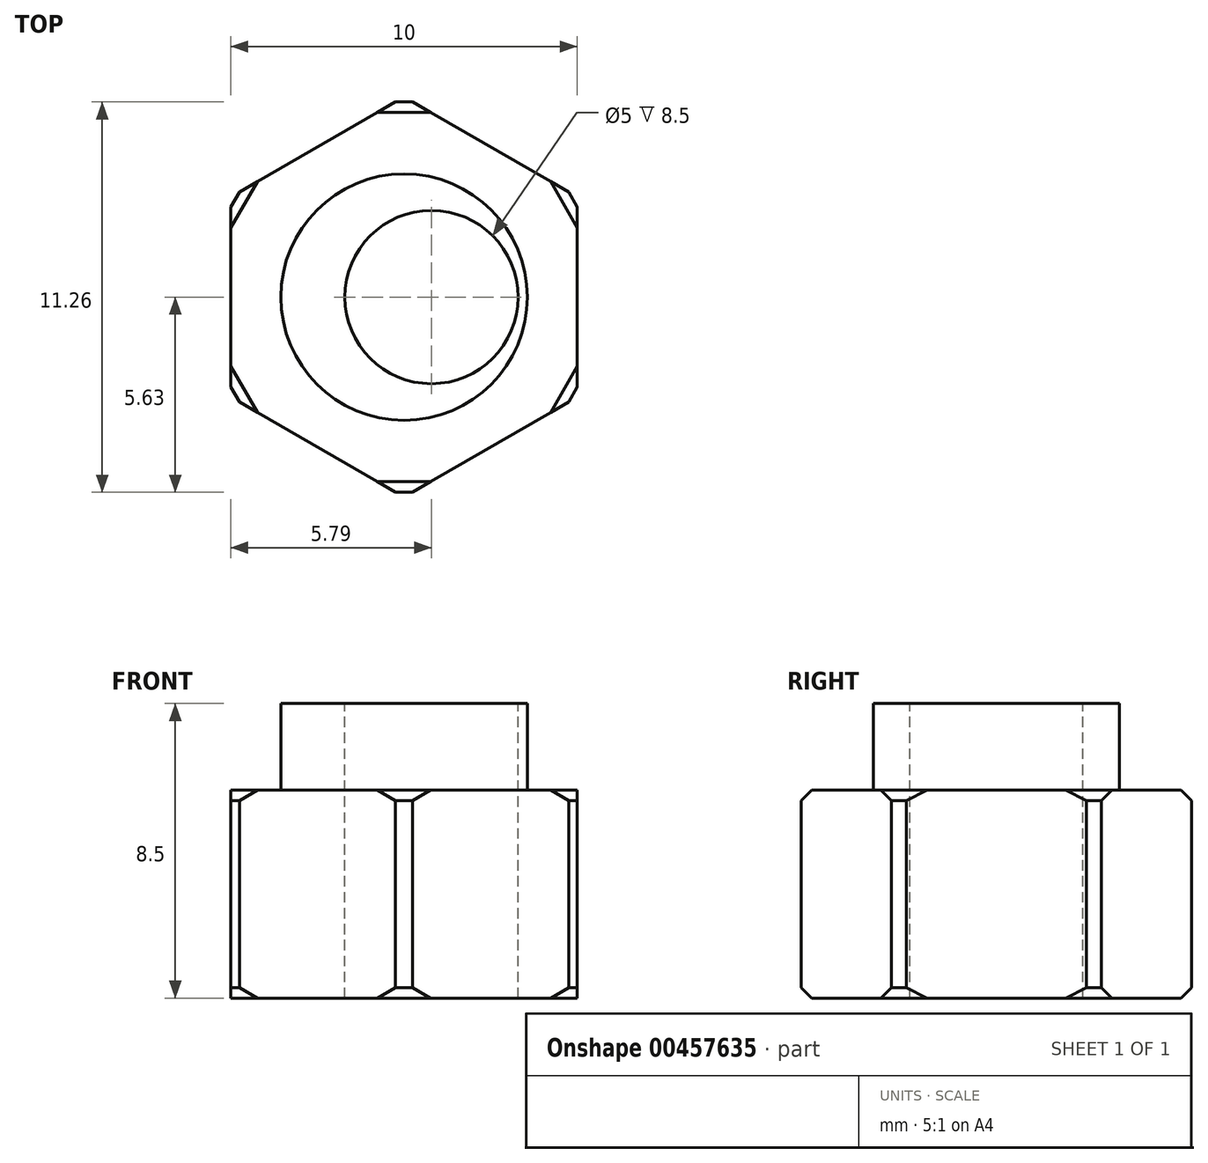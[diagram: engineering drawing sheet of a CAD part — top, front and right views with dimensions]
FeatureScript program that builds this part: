
annotation { "Feature Type Name" : "Feature", "Feature Type Description" : "" }
export const myFeature = defineFeature(function(context is Context, id is Id, definition is map)
    precondition{}
    {
        {
            var Q0;
            Q0=qCreatedBy(makeId("Top.planeOp"),FACE);
            var sketch = newSketch(context, id + "F0", { "sketchPlane" : qUnion([Q0])});
            skCircle(sketch, "E0.cCircle", {"center": v(0, 0) * mm, "radius": 5 * mm, "construction": true});
            skLineSegment(sketch, "E0.0", {"start": v(5, -2.89) * mm, "end": v(0, -5.77) * mm});
            skLineSegment(sketch, "E0.1", {"start": v(0, -5.77) * mm, "end": v(-5, -2.89) * mm});
            skLineSegment(sketch, "E0.2", {"start": v(-5, -2.89) * mm, "end": v(-5, 2.89) * mm});
            skLineSegment(sketch, "E0.3", {"start": v(-5, 2.89) * mm, "end": v(0, 5.77) * mm});
            skLineSegment(sketch, "E0.4", {"start": v(0, 5.77) * mm, "end": v(5, 2.89) * mm});
            skLineSegment(sketch, "E0.5", {"start": v(5, 2.89) * mm, "end": v(5, -2.89) * mm});
            skPoint(sketch, "E0.0.midPoint", {"position": v(2.5, -4.33) * mm});
            skSolve(sketch);
        }
        {
            var Q0;
            Q0=makeQuery(id+"F0.imprint","IMPRINT",FACE,{"disambiguationData":[TD([[makeQuery(id+"F0.imprint","IMPRINT",EDGE,{"derivedFrom":sQuery(id+"F0.wireOp",EDGE,"E0.0")}),-1.0]])]});
            extrude(context, id + "F1", {"entities" : qUnion([Q0]), "depth" : 6 * mm});
        }
        {
            var Q0;
            Q0=makeQuery(id+"F1.opExtrude","SWEPT_EDGE",EDGE,{"disambiguationData":[OSD([sQuery(id+"F0.wireOp",EDGE,"E0.4"),sQuery(id+"F0.wireOp",EDGE,"E0.5")])]});
            var Q1;
            Q1=makeQuery(id+"F1.opExtrude","SWEPT_EDGE",EDGE,{"disambiguationData":[OSD([sQuery(id+"F0.wireOp",EDGE,"E0.3"),sQuery(id+"F0.wireOp",EDGE,"E0.4")])]});
            var Q2;
            Q2=makeQuery(id+"F1.opExtrude","SWEPT_EDGE",EDGE,{"disambiguationData":[OSD([sQuery(id+"F0.wireOp",EDGE,"E0.0"),sQuery(id+"F0.wireOp",EDGE,"E0.5")])]});
            var Q3;
            Q3=makeQuery(id+"F1.opExtrude","SWEPT_EDGE",EDGE,{"disambiguationData":[OSD([sQuery(id+"F0.wireOp",EDGE,"E0.0"),sQuery(id+"F0.wireOp",EDGE,"E0.1")])]});
            var Q4;
            Q4=makeQuery(id+"F1.opExtrude","SWEPT_EDGE",EDGE,{"disambiguationData":[OSD([sQuery(id+"F0.wireOp",EDGE,"E0.1"),sQuery(id+"F0.wireOp",EDGE,"E0.2")])]});
            var Q5;
            Q5=makeQuery(id+"F1.opExtrude","SWEPT_EDGE",EDGE,{"disambiguationData":[OSD([sQuery(id+"F0.wireOp",EDGE,"E0.2"),sQuery(id+"F0.wireOp",EDGE,"E0.3")])]});
            chamfer(context, id + "F2", {"entities" : qUnion([Q0, Q1, Q2, Q3, Q4, Q5]), "width" : 0.5 * mm, "tangentPropagation" : true});
        }
        {
            var Q0;
            {var subQ0=sQuery(id+"F0.wireOp",EDGE,"E0.5");var subQ1=sQuery(id+"F0.wireOp",EDGE,"E0.4");Q0=makeQuery(id+"F2.opChamfer","BLEND_EDGE",EDGE,{"blendedFrom":[makeQuery(id+"F1.opExtrude","SWEPT_EDGE",EDGE,{"disambiguationData":[OSD([subQ1,subQ0])]}),makeQuery(id+"F1.opExtrude","CAP_FACE",FACE,{"disambiguationData":[OSD([sQuery(id+"F0.wireOp",EDGE,"E0.0"),sQuery(id+"F0.wireOp",EDGE,"E0.1"),sQuery(id+"F0.wireOp",EDGE,"E0.2"),sQuery(id+"F0.wireOp",EDGE,"E0.3"),subQ1,subQ0])],"isStart":false})],"blendedInto":[makeQuery(id+"F1.opExtrude","CAP_FACE",FACE,{"disambiguationData":[OSD([sQuery(id+"F0.wireOp",EDGE,"E0.0"),sQuery(id+"F0.wireOp",EDGE,"E0.1"),sQuery(id+"F0.wireOp",EDGE,"E0.2"),sQuery(id+"F0.wireOp",EDGE,"E0.3"),subQ1,subQ0])],"isStart":false})]});}
            var Q1;
            {var subQ0=sQuery(id+"F0.wireOp",EDGE,"E0.5");var subQ1=sQuery(id+"F0.wireOp",EDGE,"E0.0");Q1=makeQuery(id+"F2.opChamfer","BLEND_EDGE",EDGE,{"blendedFrom":[makeQuery(id+"F1.opExtrude","SWEPT_EDGE",EDGE,{"disambiguationData":[OSD([subQ1,subQ0])]}),makeQuery(id+"F1.opExtrude","CAP_FACE",FACE,{"disambiguationData":[OSD([subQ1,sQuery(id+"F0.wireOp",EDGE,"E0.1"),sQuery(id+"F0.wireOp",EDGE,"E0.2"),sQuery(id+"F0.wireOp",EDGE,"E0.3"),sQuery(id+"F0.wireOp",EDGE,"E0.4"),subQ0])],"isStart":false})],"blendedInto":[makeQuery(id+"F1.opExtrude","CAP_FACE",FACE,{"disambiguationData":[OSD([subQ1,sQuery(id+"F0.wireOp",EDGE,"E0.1"),sQuery(id+"F0.wireOp",EDGE,"E0.2"),sQuery(id+"F0.wireOp",EDGE,"E0.3"),sQuery(id+"F0.wireOp",EDGE,"E0.4"),subQ0])],"isStart":false})]});}
            var Q2;
            {var subQ0=sQuery(id+"F0.wireOp",EDGE,"E0.4");var subQ1=sQuery(id+"F0.wireOp",EDGE,"E0.3");Q2=makeQuery(id+"F2.opChamfer","BLEND_EDGE",EDGE,{"blendedFrom":[makeQuery(id+"F1.opExtrude","SWEPT_EDGE",EDGE,{"disambiguationData":[OSD([subQ1,subQ0])]}),makeQuery(id+"F1.opExtrude","CAP_FACE",FACE,{"disambiguationData":[OSD([sQuery(id+"F0.wireOp",EDGE,"E0.0"),sQuery(id+"F0.wireOp",EDGE,"E0.1"),sQuery(id+"F0.wireOp",EDGE,"E0.2"),subQ1,subQ0,sQuery(id+"F0.wireOp",EDGE,"E0.5")])],"isStart":false})],"blendedInto":[makeQuery(id+"F1.opExtrude","CAP_FACE",FACE,{"disambiguationData":[OSD([sQuery(id+"F0.wireOp",EDGE,"E0.0"),sQuery(id+"F0.wireOp",EDGE,"E0.1"),sQuery(id+"F0.wireOp",EDGE,"E0.2"),subQ1,subQ0,sQuery(id+"F0.wireOp",EDGE,"E0.5")])],"isStart":false})]});}
            var Q3;
            {var subQ0=sQuery(id+"F0.wireOp",EDGE,"E0.3");var subQ1=sQuery(id+"F0.wireOp",EDGE,"E0.2");Q3=makeQuery(id+"F2.opChamfer","BLEND_EDGE",EDGE,{"blendedFrom":[makeQuery(id+"F1.opExtrude","SWEPT_EDGE",EDGE,{"disambiguationData":[OSD([subQ1,subQ0])]}),makeQuery(id+"F1.opExtrude","CAP_FACE",FACE,{"disambiguationData":[OSD([sQuery(id+"F0.wireOp",EDGE,"E0.0"),sQuery(id+"F0.wireOp",EDGE,"E0.1"),subQ1,subQ0,sQuery(id+"F0.wireOp",EDGE,"E0.4"),sQuery(id+"F0.wireOp",EDGE,"E0.5")])],"isStart":false})],"blendedInto":[makeQuery(id+"F1.opExtrude","CAP_FACE",FACE,{"disambiguationData":[OSD([sQuery(id+"F0.wireOp",EDGE,"E0.0"),sQuery(id+"F0.wireOp",EDGE,"E0.1"),subQ1,subQ0,sQuery(id+"F0.wireOp",EDGE,"E0.4"),sQuery(id+"F0.wireOp",EDGE,"E0.5")])],"isStart":false})]});}
            var Q4;
            {var subQ0=sQuery(id+"F0.wireOp",EDGE,"E0.2");var subQ1=sQuery(id+"F0.wireOp",EDGE,"E0.1");Q4=makeQuery(id+"F2.opChamfer","BLEND_EDGE",EDGE,{"blendedFrom":[makeQuery(id+"F1.opExtrude","SWEPT_EDGE",EDGE,{"disambiguationData":[OSD([subQ1,subQ0])]}),makeQuery(id+"F1.opExtrude","CAP_FACE",FACE,{"disambiguationData":[OSD([sQuery(id+"F0.wireOp",EDGE,"E0.0"),subQ1,subQ0,sQuery(id+"F0.wireOp",EDGE,"E0.3"),sQuery(id+"F0.wireOp",EDGE,"E0.4"),sQuery(id+"F0.wireOp",EDGE,"E0.5")])],"isStart":false})],"blendedInto":[makeQuery(id+"F1.opExtrude","CAP_FACE",FACE,{"disambiguationData":[OSD([sQuery(id+"F0.wireOp",EDGE,"E0.0"),subQ1,subQ0,sQuery(id+"F0.wireOp",EDGE,"E0.3"),sQuery(id+"F0.wireOp",EDGE,"E0.4"),sQuery(id+"F0.wireOp",EDGE,"E0.5")])],"isStart":false})]});}
            var Q5;
            {var subQ0=sQuery(id+"F0.wireOp",EDGE,"E0.1");var subQ1=sQuery(id+"F0.wireOp",EDGE,"E0.0");Q5=makeQuery(id+"F2.opChamfer","BLEND_EDGE",EDGE,{"blendedFrom":[makeQuery(id+"F1.opExtrude","SWEPT_EDGE",EDGE,{"disambiguationData":[OSD([subQ1,subQ0])]}),makeQuery(id+"F1.opExtrude","CAP_FACE",FACE,{"disambiguationData":[OSD([subQ1,subQ0,sQuery(id+"F0.wireOp",EDGE,"E0.2"),sQuery(id+"F0.wireOp",EDGE,"E0.3"),sQuery(id+"F0.wireOp",EDGE,"E0.4"),sQuery(id+"F0.wireOp",EDGE,"E0.5")])],"isStart":false})],"blendedInto":[makeQuery(id+"F1.opExtrude","CAP_FACE",FACE,{"disambiguationData":[OSD([subQ1,subQ0,sQuery(id+"F0.wireOp",EDGE,"E0.2"),sQuery(id+"F0.wireOp",EDGE,"E0.3"),sQuery(id+"F0.wireOp",EDGE,"E0.4"),sQuery(id+"F0.wireOp",EDGE,"E0.5")])],"isStart":false})]});}
            var Q6;
            {var subQ0=sQuery(id+"F0.wireOp",EDGE,"E0.2");var subQ1=sQuery(id+"F0.wireOp",EDGE,"E0.1");Q6=makeQuery(id+"F2.opChamfer","BLEND_EDGE",EDGE,{"blendedFrom":[makeQuery(id+"F1.opExtrude","SWEPT_EDGE",EDGE,{"disambiguationData":[OSD([subQ1,subQ0])]}),makeQuery(id+"F1.opExtrude","CAP_FACE",FACE,{"disambiguationData":[OSD([sQuery(id+"F0.wireOp",EDGE,"E0.0"),subQ1,subQ0,sQuery(id+"F0.wireOp",EDGE,"E0.3"),sQuery(id+"F0.wireOp",EDGE,"E0.4"),sQuery(id+"F0.wireOp",EDGE,"E0.5")])],"isStart":true})],"blendedInto":[makeQuery(id+"F1.opExtrude","CAP_FACE",FACE,{"disambiguationData":[OSD([sQuery(id+"F0.wireOp",EDGE,"E0.0"),subQ1,subQ0,sQuery(id+"F0.wireOp",EDGE,"E0.3"),sQuery(id+"F0.wireOp",EDGE,"E0.4"),sQuery(id+"F0.wireOp",EDGE,"E0.5")])],"isStart":true})]});}
            var Q7;
            {var subQ0=sQuery(id+"F0.wireOp",EDGE,"E0.1");var subQ1=sQuery(id+"F0.wireOp",EDGE,"E0.0");Q7=makeQuery(id+"F2.opChamfer","BLEND_EDGE",EDGE,{"blendedFrom":[makeQuery(id+"F1.opExtrude","SWEPT_EDGE",EDGE,{"disambiguationData":[OSD([subQ1,subQ0])]}),makeQuery(id+"F1.opExtrude","CAP_FACE",FACE,{"disambiguationData":[OSD([subQ1,subQ0,sQuery(id+"F0.wireOp",EDGE,"E0.2"),sQuery(id+"F0.wireOp",EDGE,"E0.3"),sQuery(id+"F0.wireOp",EDGE,"E0.4"),sQuery(id+"F0.wireOp",EDGE,"E0.5")])],"isStart":true})],"blendedInto":[makeQuery(id+"F1.opExtrude","CAP_FACE",FACE,{"disambiguationData":[OSD([subQ1,subQ0,sQuery(id+"F0.wireOp",EDGE,"E0.2"),sQuery(id+"F0.wireOp",EDGE,"E0.3"),sQuery(id+"F0.wireOp",EDGE,"E0.4"),sQuery(id+"F0.wireOp",EDGE,"E0.5")])],"isStart":true})]});}
            var Q8;
            {var subQ0=sQuery(id+"F0.wireOp",EDGE,"E0.5");var subQ1=sQuery(id+"F0.wireOp",EDGE,"E0.0");Q8=makeQuery(id+"F2.opChamfer","BLEND_EDGE",EDGE,{"blendedFrom":[makeQuery(id+"F1.opExtrude","SWEPT_EDGE",EDGE,{"disambiguationData":[OSD([subQ1,subQ0])]}),makeQuery(id+"F1.opExtrude","CAP_FACE",FACE,{"disambiguationData":[OSD([subQ1,sQuery(id+"F0.wireOp",EDGE,"E0.1"),sQuery(id+"F0.wireOp",EDGE,"E0.2"),sQuery(id+"F0.wireOp",EDGE,"E0.3"),sQuery(id+"F0.wireOp",EDGE,"E0.4"),subQ0])],"isStart":true})],"blendedInto":[makeQuery(id+"F1.opExtrude","CAP_FACE",FACE,{"disambiguationData":[OSD([subQ1,sQuery(id+"F0.wireOp",EDGE,"E0.1"),sQuery(id+"F0.wireOp",EDGE,"E0.2"),sQuery(id+"F0.wireOp",EDGE,"E0.3"),sQuery(id+"F0.wireOp",EDGE,"E0.4"),subQ0])],"isStart":true})]});}
            var Q9;
            {var subQ0=sQuery(id+"F0.wireOp",EDGE,"E0.5");var subQ1=sQuery(id+"F0.wireOp",EDGE,"E0.4");Q9=makeQuery(id+"F2.opChamfer","BLEND_EDGE",EDGE,{"blendedFrom":[makeQuery(id+"F1.opExtrude","SWEPT_EDGE",EDGE,{"disambiguationData":[OSD([subQ1,subQ0])]}),makeQuery(id+"F1.opExtrude","CAP_FACE",FACE,{"disambiguationData":[OSD([sQuery(id+"F0.wireOp",EDGE,"E0.0"),sQuery(id+"F0.wireOp",EDGE,"E0.1"),sQuery(id+"F0.wireOp",EDGE,"E0.2"),sQuery(id+"F0.wireOp",EDGE,"E0.3"),subQ1,subQ0])],"isStart":true})],"blendedInto":[makeQuery(id+"F1.opExtrude","CAP_FACE",FACE,{"disambiguationData":[OSD([sQuery(id+"F0.wireOp",EDGE,"E0.0"),sQuery(id+"F0.wireOp",EDGE,"E0.1"),sQuery(id+"F0.wireOp",EDGE,"E0.2"),sQuery(id+"F0.wireOp",EDGE,"E0.3"),subQ1,subQ0])],"isStart":true})]});}
            var Q10;
            {var subQ0=sQuery(id+"F0.wireOp",EDGE,"E0.4");var subQ1=sQuery(id+"F0.wireOp",EDGE,"E0.3");Q10=makeQuery(id+"F2.opChamfer","BLEND_EDGE",EDGE,{"blendedFrom":[makeQuery(id+"F1.opExtrude","SWEPT_EDGE",EDGE,{"disambiguationData":[OSD([subQ1,subQ0])]}),makeQuery(id+"F1.opExtrude","CAP_FACE",FACE,{"disambiguationData":[OSD([sQuery(id+"F0.wireOp",EDGE,"E0.0"),sQuery(id+"F0.wireOp",EDGE,"E0.1"),sQuery(id+"F0.wireOp",EDGE,"E0.2"),subQ1,subQ0,sQuery(id+"F0.wireOp",EDGE,"E0.5")])],"isStart":true})],"blendedInto":[makeQuery(id+"F1.opExtrude","CAP_FACE",FACE,{"disambiguationData":[OSD([sQuery(id+"F0.wireOp",EDGE,"E0.0"),sQuery(id+"F0.wireOp",EDGE,"E0.1"),sQuery(id+"F0.wireOp",EDGE,"E0.2"),subQ1,subQ0,sQuery(id+"F0.wireOp",EDGE,"E0.5")])],"isStart":true})]});}
            var Q11;
            {var subQ0=sQuery(id+"F0.wireOp",EDGE,"E0.3");var subQ1=sQuery(id+"F0.wireOp",EDGE,"E0.2");Q11=makeQuery(id+"F2.opChamfer","BLEND_EDGE",EDGE,{"blendedFrom":[makeQuery(id+"F1.opExtrude","SWEPT_EDGE",EDGE,{"disambiguationData":[OSD([subQ1,subQ0])]}),makeQuery(id+"F1.opExtrude","CAP_FACE",FACE,{"disambiguationData":[OSD([sQuery(id+"F0.wireOp",EDGE,"E0.0"),sQuery(id+"F0.wireOp",EDGE,"E0.1"),subQ1,subQ0,sQuery(id+"F0.wireOp",EDGE,"E0.4"),sQuery(id+"F0.wireOp",EDGE,"E0.5")])],"isStart":true})],"blendedInto":[makeQuery(id+"F1.opExtrude","CAP_FACE",FACE,{"disambiguationData":[OSD([sQuery(id+"F0.wireOp",EDGE,"E0.0"),sQuery(id+"F0.wireOp",EDGE,"E0.1"),subQ1,subQ0,sQuery(id+"F0.wireOp",EDGE,"E0.4"),sQuery(id+"F0.wireOp",EDGE,"E0.5")])],"isStart":true})]});}
            chamfer(context, id + "F3", {"entities" : qUnion([Q0, Q1, Q2, Q3, Q4, Q5, Q6, Q7, Q8, Q9, Q10, Q11]), "width" : 0.3 * mm, "tangentPropagation" : true});
        }
        {
            var Q0;
            Q0=makeQuery(id+"F1.opExtrude","CAP_FACE",FACE,{"disambiguationData":[OSD([sQuery(id+"F0.wireOp",EDGE,"E0.0"),sQuery(id+"F0.wireOp",EDGE,"E0.1"),sQuery(id+"F0.wireOp",EDGE,"E0.2"),sQuery(id+"F0.wireOp",EDGE,"E0.3"),sQuery(id+"F0.wireOp",EDGE,"E0.4"),sQuery(id+"F0.wireOp",EDGE,"E0.5")])],"isStart":false});
            var sketch = newSketch(context, id + "F4", { "sketchPlane" : qUnion([Q0])});
            skCircle(sketch, "E1", {"center": v(0, 0) * mm, "radius": 3.56 * mm});
            skSolve(sketch);
        }
        {
            var Q0;
            Q0 = qSketchRegion(id + "F4", true);
            extrude(context, id + "F5", {"entities" : qUnion([Q0]), "operationType" : NewBodyOperationType.ADD, "depth" : 2.5 * mm});
        }
        {
            var Q0;
            Q0=makeQuery(id+"F5.opExtrude","CAP_FACE",FACE,{"disambiguationData":[OSD([sQuery(id+"F4.wireOp",EDGE,"E1")])],"isStart":false});
            var sketch = newSketch(context, id + "F6", { "sketchPlane" : qUnion([Q0])});
            skCircle(sketch, "E2", {"center": v(0.79, 0) * mm, "radius": 2.5 * mm});
            skSolve(sketch);
        }
        {
            var Q0;
            Q0 = qSketchRegion(id + "F6", true);
            extrude(context, id + "F7", {"entities" : qUnion([Q0]), "operationType" : NewBodyOperationType.REMOVE, "endBound" : BoundingType.THROUGH_ALL, "oppositeDirection" : true, "depth" : 25 * mm});
        }
    });
